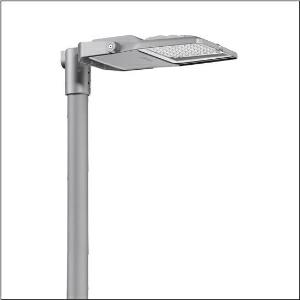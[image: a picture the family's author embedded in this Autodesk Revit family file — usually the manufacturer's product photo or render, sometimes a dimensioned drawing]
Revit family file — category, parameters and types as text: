
# Revit family: floodlight_fl_21_iq_mini___pl43_5xa7771b2a3a_6d21
name_source: partatom
category: Lighting Fixtures
units: mm (PartAtom-declared; Revit-internal decimal feet)

## family parameters
Cut with Voids When Loaded = No
Host = Face
Light Source = No
Part Type = Normal
Room Calculation Point = No
Round Connector Dimension = Use Diameter
Shared = No

## types (1)
- --- (1 x LED, 6400 lm, 45.5 W, 3000K)
    Apparent Load = 46 VA
    CIE Flux Codes = 27 78 99 100 100
    Color Rendering = 70
    Color Temperature = 3000K
    Default Elevation = 1800 mm
    Description = Floodlight FL 21 iQ mini, floodlight, primary light control with lens, of PMMA, primary optical cover: protective disc, of toughened safety glass, transparent, light distribution: PL43, light emission: direct distribution, installation type: surface-mounted, LED, High Power LED, rated luminous flux: 6.400lm, luminous efficacy: 141lm/W, light colour: 730, colour temperature: 3000K, control: Auto-Match, Temp-Guard, Lumen-Switch, Night-Set, Smart-Wire, Light-Fading, Desk-Remote (wireless, voltage-free reading and setting of iQ features in the workshop via application-optimized NFC function/RFID function), optimised constant luminous flux control (CLO 2.0), with terminal, 6-pole, mains connection: 220..240V, AC, 50/60Hz, start of lifetime: 46W, end of service life: 48W, reduction: 22W, luminaire housing, of diecast aluminium, powder-coated, Siteco® metallic grey (DB 702S), corrosivity category C5 mid according to DIN EN ISO 12944, sealing non-destructively replaceable, please order mast flange separately, mast bracket, of steel, galvanised, powder-coated, Siteco® metallic grey (DB 702S), protection rating (complete): IP66, insulation class (complete): insulation class II (safety insulation), certification: CE, ENEC, VDE, protection symbol: D, impact resistance: IK08, permissible operating ambient temperature: -40..+40°C, permissible operating ambient temperature for outdoor applications: -40..+50°C, standard: DIN EN 12944, LABS conformity tested according to VDMA 24364:2018-05, packaging unit: 1 piece

Light Distribution: PL43
    Height = 70 mm
    Lamp = 1 x LED
    Lamp Light Flux = 6400 lm
    Lamp Power = 45.5 W
    Lamp count = 1
    Length = 485 mm
    Luminous efficacy = 141 lm/W
    Manufacturer = Siteco
    ModVariant = No
    Model = 5XA7771B2A3A
    Number of Poles = 1
    OnlyDefault = Yes
    Power Factor = 1
    Product Name = Floodlight FL 21 iQ mini | PL43
    Product group = floodlight | pylon annexe
    ProductGroupID = 6200
    Protection Class = Protection class II
    Protection Degree = IP 66
    RLX_Detail_Level = 1
    RLX_Emergency_Light_Flux = 0 lm
    RLX_Emergency_Type = 0
    RLX_Emergency_Type_DB = No
    RlxData = <blob elided: 101077 chars, md5=f0791643>
    Socket = socket
    Standby Power = 0 W
    System Light Flux = 6400 lm
    System Power = 46 W
    Type Comments = factory setting: luminous flux: 100 % | dim-lin: 254 | 463 mA
    Type Image = l_1007125.jpg
    URL = http://relux.com
    VarID = @adj_133339
    Voltage = 0 V
    Weight = 0.00 kg
    Width = 337 mm

## geometry (parser evidence)
native form markers: Blend x4, Sweep x11
no freeform markers — native parametric forms only
